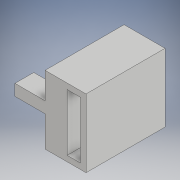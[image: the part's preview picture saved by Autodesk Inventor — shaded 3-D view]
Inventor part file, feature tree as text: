
AUTODESK INVENTOR PART (.ipt)
format: ipt  version: 2017 (Build 210142000, 142)  size: 115,712 bytes
history: native  units: in
note: dims shown in document units (in); Inventor stores cm internally (conversion verified against a paired STEP export)
features: extrude x3, sketch x3, projected_geometry x2
ambient origin geometry x8: Origin, YZ Plane, XZ Plane, XY Plane, X Axis, Y Axis, Z Axis, Center Point
bodies: Solid1 (feature_tree)
feature tree (8):
  extrude  "Extrusion1"  Depth=5.44in
  extrude  "Extrusion2"  Depth=0.75in
  extrude  "Extrusion3"  Depth=0.75in
  sketch  "Sketch1"  dims[d0=9.063in d1=5.44in]
  sketch  "Sketch2"  dims[d2=10.5in d3=0.0in d4=0.75in]
  projected_geometry  "Projected Loop1"
  sketch  "Sketch3"  dims[d5=2.5in d7=0.75in d8=10.5in d9=0.0in d11=4.0in d12=1.5in d14=5.0in d15=2.5in d16=0.0in d17=0.75in]
  projected_geometry  "Projected Loop2"
